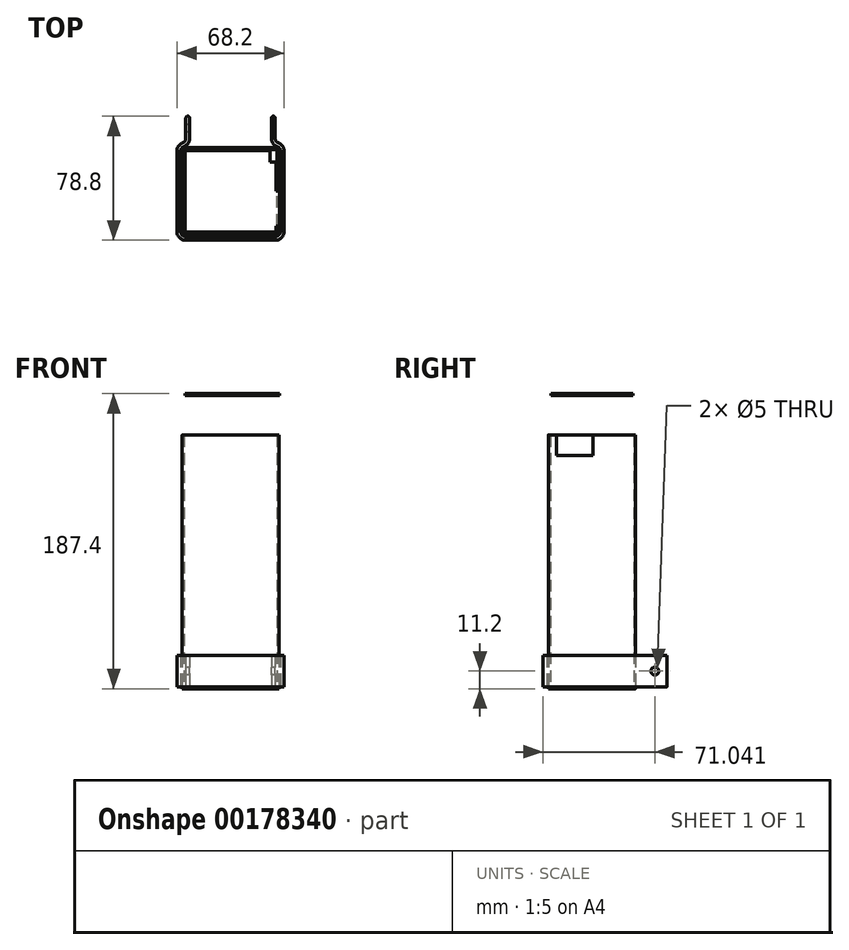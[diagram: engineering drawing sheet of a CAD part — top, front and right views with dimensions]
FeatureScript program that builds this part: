
annotation { "Feature Type Name" : "Feature", "Feature Type Description" : "" }
export const myFeature = defineFeature(function(context is Context, id is Id, definition is map)
    precondition{}
    {
        {
            var Q0;
            Q0=qCreatedBy(makeId("Top.planeOp"),FACE);
            var sketch = newSketch(context, id + "F0", { "sketchPlane" : qUnion([Q0])});
            skLineSegment(sketch, "E0.bottom", {"start": v(28.5, -26.5) * mm, "end": v(-28.5, -26.5) * mm});
            skLineSegment(sketch, "E0.top", {"start": v(28.5, 26.5) * mm, "end": v(-28.5, 26.5) * mm});
            skLineSegment(sketch, "E0.left", {"start": v(29.5, -25.5) * mm, "end": v(29.5, 25.5) * mm});
            skLineSegment(sketch, "E0.right", {"start": v(-29.5, -25.5) * mm, "end": v(-29.5, 25.5) * mm});
            skPoint(sketch, "E0.middle", {"position": v(0, 0) * mm});
            skPoint(sketch, "E1.visualSharp", {"position": v(-29.5, 26.5) * mm});
            skArc(sketch, "E1.filletArc", {"start": v(-28.5, 26.5) * mm, "mid": v(-29.2, 26.2) * mm, "end": v(-29.5, 25.5) * mm});
            skPoint(sketch, "E2.visualSharp", {"position": v(29.5, 26.5) * mm});
            skArc(sketch, "E2.filletArc", {"start": v(29.5, 25.5) * mm, "mid": v(29.2, 26.2) * mm, "end": v(28.5, 26.5) * mm});
            skPoint(sketch, "E3.visualSharp", {"position": v(29.5, -26.5) * mm});
            skArc(sketch, "E3.filletArc", {"start": v(28.5, -26.5) * mm, "mid": v(29.2, -26.2) * mm, "end": v(29.5, -25.5) * mm});
            skPoint(sketch, "E4.visualSharp", {"position": v(-29.5, -26.5) * mm});
            skArc(sketch, "E4.filletArc", {"start": v(-29.5, -25.5) * mm, "mid": v(-29.2, -26.2) * mm, "end": v(-28.5, -26.5) * mm});
            skArc(sketch, "E5.0", {"start": v(-30.7, -25.5) * mm, "mid": v(-30.06, -27.06) * mm, "end": v(-28.5, -27.7) * mm});
            skLineSegment(sketch, "E5.1", {"start": v(28.5, -27.7) * mm, "end": v(-28.5, -27.7) * mm});
            skLineSegment(sketch, "E5.2", {"start": v(-30.7, -25.5) * mm, "end": v(-30.7, 25.5) * mm});
            skArc(sketch, "E5.3", {"start": v(28.5, -27.7) * mm, "mid": v(30.06, -27.06) * mm, "end": v(30.7, -25.5) * mm});
            skArc(sketch, "E5.4", {"start": v(-28.5, 27.7) * mm, "mid": v(-30.06, 27.06) * mm, "end": v(-30.7, 25.5) * mm});
            skLineSegment(sketch, "E5.5", {"start": v(28.5, 27.7) * mm, "end": v(-28.5, 27.7) * mm});
            skArc(sketch, "E5.6", {"start": v(30.7, 25.5) * mm, "mid": v(30.06, 27.06) * mm, "end": v(28.5, 27.7) * mm});
            skLineSegment(sketch, "E5.7", {"start": v(30.7, -25.5) * mm, "end": v(30.7, 25.5) * mm});
            skArc(sketch, "E6.0", {"start": v(31.7, 25.5) * mm, "mid": v(31.1, 27.38) * mm, "end": v(29.5, 28.54) * mm});
            skLineSegment(sketch, "E6.1", {"start": v(31.7, -25.5) * mm, "end": v(31.7, 25.5) * mm});
            skLineSegment(sketch, "E6.2", {"start": v(26, 28.7) * mm, "end": v(26, 28.7) * mm});
            skArc(sketch, "E6.3", {"start": v(28.5, -28.7) * mm, "mid": v(30.76, -27.76) * mm, "end": v(31.7, -25.5) * mm});
            skArc(sketch, "E6.4", {"start": v(-29.5, 28.54) * mm, "mid": v(-31.1, 27.38) * mm, "end": v(-31.7, 25.5) * mm});
            skLineSegment(sketch, "E6.5", {"start": v(-31.7, -25.5) * mm, "end": v(-31.7, 25.5) * mm});
            skArc(sketch, "E6.6", {"start": v(-31.7, -25.5) * mm, "mid": v(-30.76, -27.76) * mm, "end": v(-28.5, -28.7) * mm});
            skLineSegment(sketch, "E6.7", {"start": v(28.5, -28.7) * mm, "end": v(-28.5, -28.7) * mm});
            skLineSegment(sketch, "E7", {"start": v(-26, 47.7) * mm, "end": v(-26, 33.38) * mm});
            skLineSegment(sketch, "E8", {"start": v(26, 47.7) * mm, "end": v(26, 33.38) * mm});
            skLineSegment(sketch, "E9.trimOffspring", {"start": v(-28.5, 28.7) * mm, "end": v(-28.5, 28.7) * mm});
            skLineSegment(sketch, "E10.0", {"start": v(28.4, 47.7) * mm, "end": v(28.4, 33.38) * mm});
            skArc(sketch, "E10.1", {"start": v(34.1, 25.5) * mm, "mid": v(33.04, 28.78) * mm, "end": v(30.25, 30.82) * mm});
            skLineSegment(sketch, "E10.2", {"start": v(34.1, -25.5) * mm, "end": v(34.1, 25.5) * mm});
            skArc(sketch, "E10.3", {"start": v(28.5, -31.1) * mm, "mid": v(32.46, -29.46) * mm, "end": v(34.1, -25.5) * mm});
            skLineSegment(sketch, "E10.4", {"start": v(28.5, -31.1) * mm, "end": v(-28.5, -31.1) * mm});
            skLineSegment(sketch, "E10.5", {"start": v(-28.4, 47.7) * mm, "end": v(-28.4, 33.38) * mm});
            skArc(sketch, "E10.6", {"start": v(-30.25, 30.82) * mm, "mid": v(-33.04, 28.78) * mm, "end": v(-34.1, 25.5) * mm});
            skLineSegment(sketch, "E10.7", {"start": v(-34.1, -25.5) * mm, "end": v(-34.1, 25.5) * mm});
            skArc(sketch, "E10.8", {"start": v(-34.1, -25.5) * mm, "mid": v(-32.46, -29.46) * mm, "end": v(-28.5, -31.1) * mm});
            skLineSegment(sketch, "E11", {"start": v(-26, 47.7) * mm, "end": v(-28.4, 47.7) * mm});
            skLineSegment(sketch, "E12", {"start": v(28.4, 47.7) * mm, "end": v(26, 47.7) * mm});
            skPoint(sketch, "E13.visualSharp", {"position": v(-28.5, 28.7) * mm});
            skArc(sketch, "E13.filletArc", {"start": v(-29.5, 28.54) * mm, "mid": v(-26.97, 30.4) * mm, "end": v(-26, 33.38) * mm});
            skPoint(sketch, "E14.visualSharp", {"position": v(-28.4, 31.1) * mm});
            skArc(sketch, "E14.filletArc", {"start": v(-30.25, 30.82) * mm, "mid": v(-28.91, 31.8) * mm, "end": v(-28.4, 33.38) * mm});
            skPoint(sketch, "E15.visualSharp", {"position": v(28.4, 31.1) * mm});
            skArc(sketch, "E15.filletArc", {"start": v(28.4, 33.38) * mm, "mid": v(28.91, 31.8) * mm, "end": v(30.25, 30.82) * mm});
            skPoint(sketch, "E16.visualSharp", {"position": v(26, 27.5) * mm});
            skArc(sketch, "E16.filletArc", {"start": v(26, 33.38) * mm, "mid": v(26.97, 30.4) * mm, "end": v(29.5, 28.54) * mm});
            skSolve(sketch);
        }
        {
            var Q0;
            Q0=makeQuery(id+"F0.imprint","IMPRINT",FACE,{"disambiguationData":[TD([[makeQuery(id+"F0.imprint","IMPRINT",EDGE,{"derivedFrom":sQuery(id+"F0.wireOp",EDGE,"E0.bottom")}),1.0]])]});
            extrude(context, id + "F1", {"entities" : qUnion([Q0]), "offsetDistance" : 25 * mm, "depth" : 160 * mm, "hasSecondDirection" : true, "secondDirectionOppositeDirection" : true, "secondDirectionDepth" : 1.2 * mm});
        }
        {
            var Q0;
            Q0=makeQuery(id+"F0.imprint","IMPRINT",FACE,{"disambiguationData":[TD([[makeQuery(id+"F0.imprint","IMPRINT",EDGE,{"derivedFrom":sQuery(id+"F0.wireOp",EDGE,"E0.bottom")}),-1.0]])]});
            extrude(context, id + "F2", {"entities" : qUnion([Q0]), "operationType" : NewBodyOperationType.ADD, "oppositeDirection" : true, "depth" : 1.2 * mm});
        }
        {
            var Q0;
            Q0=makeQuery(id+"F1.opExtrude","SWEPT_FACE",FACE,{"disambiguationData":[OSD([sQuery(id+"F0.wireOp",EDGE,"E5.7")])]});
            var sketch = newSketch(context, id + "F3", { "sketchPlane" : qUnion([Q0])});
            skLineSegment(sketch, "E17.bottom", {"start": v(-22.5, 160) * mm, "end": v(0.5, 160) * mm});
            skLineSegment(sketch, "E17.top", {"start": v(-22.5, 147) * mm, "end": v(0.5, 147) * mm});
            skLineSegment(sketch, "E17.left", {"start": v(-22.5, 160) * mm, "end": v(-22.5, 147) * mm});
            skLineSegment(sketch, "E17.right", {"start": v(0.5, 160) * mm, "end": v(0.5, 147) * mm});
            skSolve(sketch);
        }
        {
            var Q0;
            Q0=makeQuery(id+"F3.imprint","IMPRINT",FACE,{"disambiguationData":[TD([[makeQuery(id+"F3.imprint","IMPRINT",EDGE,{"derivedFrom":sQuery(id+"F3.wireOp",EDGE,"E17.bottom")}),-1.0]])]});
            extrude(context, id + "F4", {"entities" : qUnion([Q0]), "operationType" : NewBodyOperationType.REMOVE, "endBound" : BoundingType.UP_TO_NEXT, "oppositeDirection" : true, "depth" : 25 * mm});
        }
        {
            var Q0;
            Q0=makeQuery(id+"F1.opExtrude","CAP_FACE",FACE,{"disambiguationData":[OSD([sQuery(id+"F0.wireOp",EDGE,"E0.bottom"),sQuery(id+"F0.wireOp",EDGE,"E0.top"),sQuery(id+"F0.wireOp",EDGE,"E0.left"),sQuery(id+"F0.wireOp",EDGE,"E0.right"),sQuery(id+"F0.wireOp",EDGE,"E1.filletArc"),sQuery(id+"F0.wireOp",EDGE,"E2.filletArc"),sQuery(id+"F0.wireOp",EDGE,"E3.filletArc"),sQuery(id+"F0.wireOp",EDGE,"E4.filletArc"),sQuery(id+"F0.wireOp",EDGE,"E5.0"),sQuery(id+"F0.wireOp",EDGE,"E5.1"),sQuery(id+"F0.wireOp",EDGE,"E5.2"),sQuery(id+"F0.wireOp",EDGE,"E5.3"),sQuery(id+"F0.wireOp",EDGE,"E5.4"),sQuery(id+"F0.wireOp",EDGE,"E5.5"),sQuery(id+"F0.wireOp",EDGE,"E5.6"),sQuery(id+"F0.wireOp",EDGE,"E5.7")])],"isStart":false});
            cPlane(context, id + "F5", {"entities" : qUnion([Q0]), "cplaneType" : CPlaneType.OFFSET, "offset" : 25 * mm, "width" : 150 * mm, "height" : 150 * mm});
        }
        {
            var Q0;
            Q0=qCreatedBy(id+"F5.planeOp",FACE);
            var sketch = newSketch(context, id + "F6", { "sketchPlane" : qUnion([Q0])});
            skArc(sketch, "E18.0.0", {"start": v(29.5, 25.5) * mm, "mid": v(29.2, 26.2) * mm, "end": v(28.5, 26.5) * mm});
            skLineSegment(sketch, "E18.0.1", {"start": v(28.5, 26.5) * mm, "end": v(-28.5, 26.5) * mm});
            skArc(sketch, "E18.0.2", {"start": v(-28.5, 26.5) * mm, "mid": v(-29.2, 26.2) * mm, "end": v(-29.5, 25.5) * mm});
            skLineSegment(sketch, "E18.0.3", {"start": v(-29.5, 25.5) * mm, "end": v(-29.5, -25.5) * mm});
            skArc(sketch, "E18.0.4", {"start": v(-29.5, -25.5) * mm, "mid": v(-29.2, -26.2) * mm, "end": v(-28.5, -26.5) * mm});
            skLineSegment(sketch, "E18.0.5", {"start": v(-28.5, -26.5) * mm, "end": v(28.5, -26.5) * mm});
            skArc(sketch, "E18.0.6", {"start": v(28.5, -26.5) * mm, "mid": v(29.2, -26.2) * mm, "end": v(29.5, -25.5) * mm});
            skLineSegment(sketch, "E18.0.7", {"start": v(29.5, -25.5) * mm, "end": v(29.5, 25.5) * mm});
            skLineSegment(sketch, "E19.0", {"start": v(29, 26) * mm, "end": v(-29, 26) * mm});
            skLineSegment(sketch, "E19.1", {"start": v(29, -26) * mm, "end": v(29, 26) * mm});
            skLineSegment(sketch, "E19.2", {"start": v(-29, -26) * mm, "end": v(29, -26) * mm});
            skLineSegment(sketch, "E19.3", {"start": v(-29, 26) * mm, "end": v(-29, -26) * mm});
            skLineSegment(sketch, "E20.bottom", {"start": v(29, 26) * mm, "end": v(25, 26) * mm});
            skLineSegment(sketch, "E20.top", {"start": v(29, 18.5) * mm, "end": v(25, 18.5) * mm});
            skLineSegment(sketch, "E20.left", {"start": v(29, 26) * mm, "end": v(29, 18.5) * mm});
            skLineSegment(sketch, "E20.right", {"start": v(25, 26) * mm, "end": v(25, 18.5) * mm});
            skLineSegment(sketch, "E21", {"start": v(29, 0) * mm, "end": v(31, 0) * mm});
            skLineSegment(sketch, "E22", {"start": v(31, 0) * mm, "end": v(31, -22) * mm});
            skLineSegment(sketch, "E23", {"start": v(31, -22) * mm, "end": v(29, -22) * mm});
            skSolve(sketch);
        }
        {
            var Q0;
            {var subQ4=sQuery(id+"F6.wireOp",EDGE,"E19.2");Q0=makeQuery(id+"F6.imprint","IMPRINT",FACE,{"disambiguationData":[TD([[makeQuery(id+"F6.imprint","IMPRINT",EDGE,{"derivedFrom":subQ4}),1.0]])]});}
            var Q1;
            {var subQ0=sQuery(id+"F6.wireOp",EDGE,"E21");var subQ1=sQuery(id+"F6.wireOp",EDGE,"E18.0.7");var subQ2=makeQuery(id+"F6.imprint","INTERSECT",VERTEX,{"derivedFrom":[subQ1,subQ0]});Q1=makeQuery(id+"F6.imprint","IMPRINT",FACE,{"disambiguationData":[TD([[makeQuery(id+"F6.imprint","IMPRINT",EDGE,{"disambiguationData":[TD([[subQ2,1.0]])],"derivedFrom":subQ1}),1.0]])]});}
            var Q2;
            {var subQ5=sQuery(id+"F6.wireOp",EDGE,"E22");Q2=makeQuery(id+"F6.imprint","IMPRINT",FACE,{"disambiguationData":[TD([[makeQuery(id+"F6.imprint","IMPRINT",EDGE,{"derivedFrom":subQ5}),-1.0]])]});}
            extrude(context, id + "F7", {"entities" : qUnion([Q0, Q1, Q2]), "depth" : 1.2 * mm});
        }
        {
            var Q0;
            Q0=makeQuery(id+"F0.imprint","IMPRINT",FACE,{"disambiguationData":[TD([[makeQuery(id+"F0.imprint","IMPRINT",EDGE,{"derivedFrom":sQuery(id+"F0.wireOp",EDGE,"E6.0")}),-1.0]])]});
            extrude(context, id + "F8", {"entities" : qUnion([Q0]), "depth" : 20 * mm, "offsetDistance" : 25 * mm});
        }
        {
            var Q0;
            Q0=makeQuery(id+"F8.opExtrude","SWEPT_EDGE",EDGE,{"disambiguationData":[OSD([sQuery(id+"F0.wireOp",EDGE,"E10.5"),sQuery(id+"F0.wireOp",EDGE,"E11")])]});
            var Q1;
            Q1=makeQuery(id+"F8.opExtrude","SWEPT_EDGE",EDGE,{"disambiguationData":[OSD([sQuery(id+"F0.wireOp",EDGE,"E7"),sQuery(id+"F0.wireOp",EDGE,"E11")])]});
            var Q2;
            Q2=makeQuery(id+"F8.opExtrude","SWEPT_EDGE",EDGE,{"disambiguationData":[OSD([sQuery(id+"F0.wireOp",EDGE,"E10.0"),sQuery(id+"F0.wireOp",EDGE,"E12")])]});
            var Q3;
            Q3=makeQuery(id+"F8.opExtrude","SWEPT_EDGE",EDGE,{"disambiguationData":[OSD([sQuery(id+"F0.wireOp",EDGE,"E8"),sQuery(id+"F0.wireOp",EDGE,"E12")])]});
            fillet(context, id + "F9", {"entities" : qUnion([Q0, Q1, Q2, Q3]), "radius" : 1.2 * mm, "tangentPropagation" : true, "allowEdgeOverflow" : false});
        }
        {
            var Q0;
            Q0=makeQuery(id+"F8.opExtrude","SWEPT_FACE",FACE,{"disambiguationData":[OSD([sQuery(id+"F0.wireOp",EDGE,"E10.5")])]});
            var sketch = newSketch(context, id + "F10", { "sketchPlane" : qUnion([Q0])});
            skCircle(sketch, "E24", {"center": v(-39.94, 10) * mm, "radius": 2.5 * mm});
            skPoint(sketch, "E24.centerSnap0", {"position": v(-46.5, 10) * mm});
            skPoint(sketch, "E24.centerSnap1", {"position": v(-39.94, 20) * mm});
            skSolve(sketch);
        }
        {
            var Q0;
            Q0=makeQuery(id+"F10.imprint","IMPRINT",FACE,{"disambiguationData":[TD([[makeQuery(id+"F10.imprint","IMPRINT",EDGE,{"derivedFrom":sQuery(id+"F10.wireOp",EDGE,"E24")}),1.0]])]});
            extrude(context, id + "F11", {"entities" : qUnion([Q0]), "operationType" : NewBodyOperationType.REMOVE, "endBound" : BoundingType.THROUGH_ALL, "oppositeDirection" : true, "depth" : 25 * mm, "offsetDistance" : 25 * mm});
        }
    });
